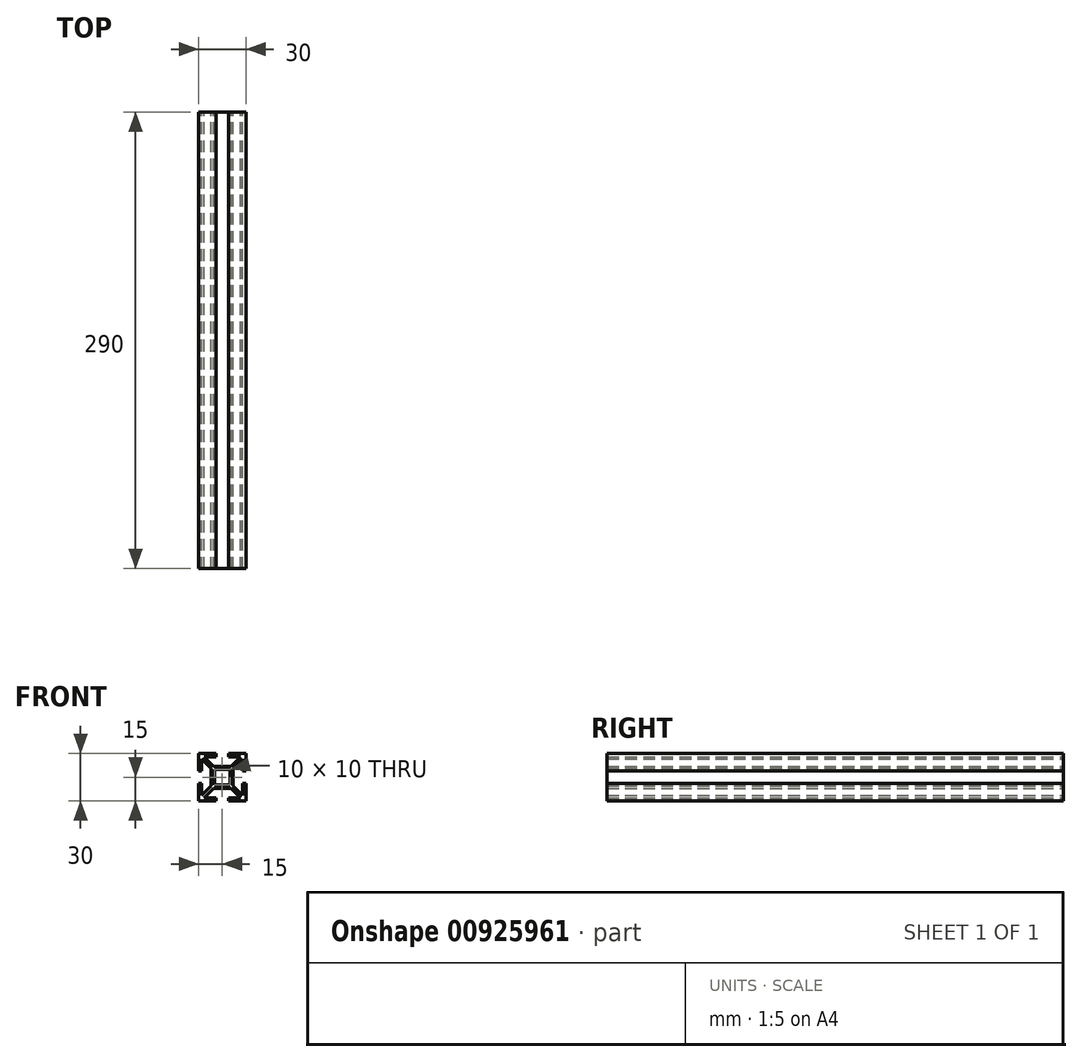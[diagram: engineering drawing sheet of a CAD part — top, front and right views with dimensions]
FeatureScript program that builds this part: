
annotation { "Feature Type Name" : "Feature", "Feature Type Description" : "" }
export const myFeature = defineFeature(function(context is Context, id is Id, definition is map)
    precondition{}
    {
        {
            var Q0;
            Q0=qCreatedBy(makeId("Front.planeOp"),FACE);
            var sketch = newSketch(context, id + "F0", { "sketchPlane" : qUnion([Q0])});
            skLineSegment(sketch, "E0.bottom", {"start": v(5, 5) * mm, "end": v(-5, 5) * mm});
            skLineSegment(sketch, "E0.top", {"start": v(5, -5) * mm, "end": v(-5, -5) * mm});
            skLineSegment(sketch, "E0.left", {"start": v(5, 5) * mm, "end": v(5, -5) * mm});
            skLineSegment(sketch, "E0.right", {"start": v(-5, 5) * mm, "end": v(-5, -5) * mm});
            skPoint(sketch, "E0.middle", {"position": v(0, 0) * mm});
            skLineSegment(sketch, "E1.0", {"start": v(7, -7) * mm, "end": v(-7, -7) * mm});
            skLineSegment(sketch, "E1.1", {"start": v(7, 7) * mm, "end": v(7, -7) * mm});
            skLineSegment(sketch, "E1.2", {"start": v(7, 7) * mm, "end": v(-7, 7) * mm});
            skLineSegment(sketch, "E1.3", {"start": v(-7, 7) * mm, "end": v(-7, -7) * mm});
            skLineSegment(sketch, "E2", {"start": v(-7, 7) * mm, "end": v(-13.08, 13.08) * mm, "construction": true});
            skLineSegment(sketch, "E3", {"start": v(-7, 5.59) * mm, "end": v(-13, 11.59) * mm});
            skLineSegment(sketch, "E4", {"start": v(-5.59, 7) * mm, "end": v(-11.59, 13) * mm});
            skLineSegment(sketch, "E5", {"start": v(-11.59, 13) * mm, "end": v(-4, 13) * mm});
            skLineSegment(sketch, "E6", {"start": v(-4, 13) * mm, "end": v(-4, 15) * mm});
            skLineSegment(sketch, "E7", {"start": v(-4, 15) * mm, "end": v(-15, 15) * mm});
            skLineSegment(sketch, "E8", {"start": v(-15, 15) * mm, "end": v(-15, 4) * mm});
            skLineSegment(sketch, "E9", {"start": v(-15, 4) * mm, "end": v(-13, 4) * mm});
            skLineSegment(sketch, "E10", {"start": v(-13, 4) * mm, "end": v(-13, 11.59) * mm});
            skLineSegment(sketch, "E11.1.0", {"start": v(-7, -7) * mm, "end": v(-13.08, -13.08) * mm, "construction": true});
            skLineSegment(sketch, "E11.1.1", {"start": v(-15, -4) * mm, "end": v(-15, -15) * mm});
            skLineSegment(sketch, "E11.1.2", {"start": v(-4, -13) * mm, "end": v(-11.59, -13) * mm});
            skLineSegment(sketch, "E11.1.3", {"start": v(-4, -15) * mm, "end": v(-4, -13) * mm});
            skLineSegment(sketch, "E11.1.4", {"start": v(-5.59, -7) * mm, "end": v(-11.59, -13) * mm});
            skLineSegment(sketch, "E11.1.5", {"start": v(-13, -4) * mm, "end": v(-15, -4) * mm});
            skLineSegment(sketch, "E11.1.6", {"start": v(-15, -15) * mm, "end": v(-4, -15) * mm});
            skLineSegment(sketch, "E11.1.7", {"start": v(-7, -5.59) * mm, "end": v(-13, -11.59) * mm});
            skLineSegment(sketch, "E11.1.8", {"start": v(-13, -11.59) * mm, "end": v(-13, -4) * mm});
            skLineSegment(sketch, "E11.2.0", {"start": v(7, -7) * mm, "end": v(13.08, -13.08) * mm, "construction": true});
            skLineSegment(sketch, "E11.2.1", {"start": v(4, -15) * mm, "end": v(15, -15) * mm});
            skLineSegment(sketch, "E11.2.2", {"start": v(13, -4) * mm, "end": v(13, -11.59) * mm});
            skLineSegment(sketch, "E11.2.3", {"start": v(15, -4) * mm, "end": v(13, -4) * mm});
            skLineSegment(sketch, "E11.2.4", {"start": v(7, -5.59) * mm, "end": v(13, -11.59) * mm});
            skLineSegment(sketch, "E11.2.5", {"start": v(4, -13) * mm, "end": v(4, -15) * mm});
            skLineSegment(sketch, "E11.2.6", {"start": v(15, -15) * mm, "end": v(15, -4) * mm});
            skLineSegment(sketch, "E11.2.7", {"start": v(5.59, -7) * mm, "end": v(11.59, -13) * mm});
            skLineSegment(sketch, "E11.2.8", {"start": v(11.59, -13) * mm, "end": v(4, -13) * mm});
            skLineSegment(sketch, "E11.3.0", {"start": v(7, 7) * mm, "end": v(13.08, 13.08) * mm, "construction": true});
            skLineSegment(sketch, "E11.3.1", {"start": v(15, 4) * mm, "end": v(15, 15) * mm});
            skLineSegment(sketch, "E11.3.2", {"start": v(4, 13) * mm, "end": v(11.59, 13) * mm});
            skLineSegment(sketch, "E11.3.3", {"start": v(4, 15) * mm, "end": v(4, 13) * mm});
            skLineSegment(sketch, "E11.3.4", {"start": v(5.59, 7) * mm, "end": v(11.59, 13) * mm});
            skLineSegment(sketch, "E11.3.5", {"start": v(13, 4) * mm, "end": v(15, 4) * mm});
            skLineSegment(sketch, "E11.3.6", {"start": v(15, 15) * mm, "end": v(4, 15) * mm});
            skLineSegment(sketch, "E11.3.7", {"start": v(7, 5.59) * mm, "end": v(13, 11.59) * mm});
            skLineSegment(sketch, "E11.3.8", {"start": v(13, 11.59) * mm, "end": v(13, 4) * mm});
            skSolve(sketch);
        }
        {
            var Q0;
            Q0=qSketchRegion(id+"F0",true);
            extrude(context, id + "F1", {"entities" : qUnion([Q0]), "endBound" : BoundingType.SYMMETRIC, "depth" : 290 * mm, "offsetDistance" : 25 * mm});
        }
    });
